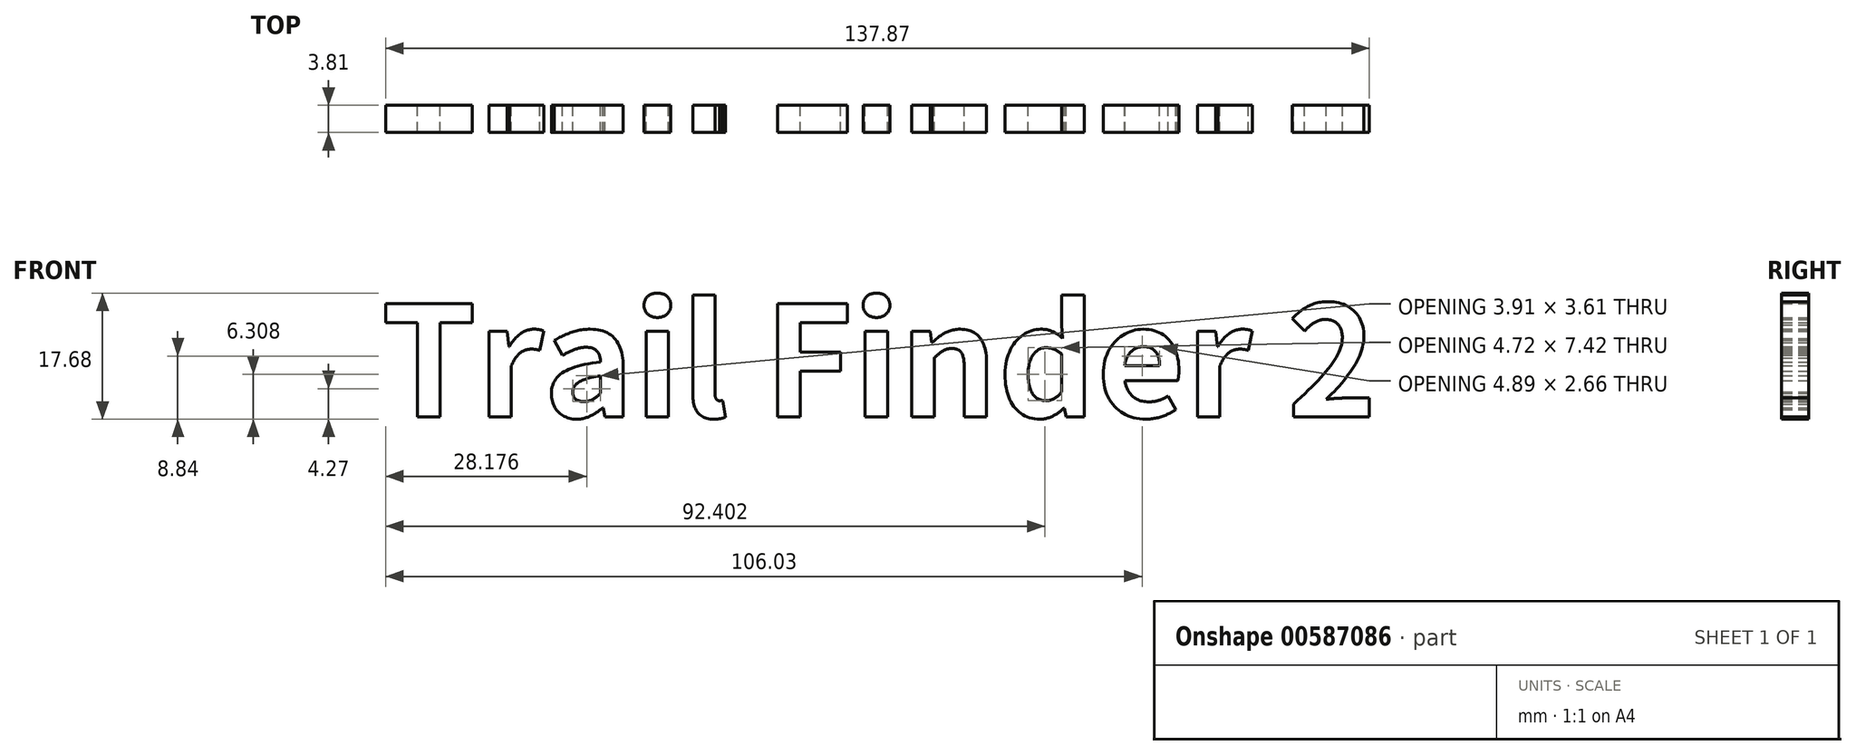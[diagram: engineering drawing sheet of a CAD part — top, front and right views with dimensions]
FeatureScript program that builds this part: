
annotation { "Feature Type Name" : "Feature", "Feature Type Description" : "" }
export const myFeature = defineFeature(function(context is Context, id is Id, definition is map)
    precondition{}
    {
        {
            var Q0;
            Q0=qCreatedBy(makeId("Front.planeOp"),FACE);
            var sketch = newSketch(context, id + "F0", { "sketchPlane" : qUnion([Q0])});
            skText(sketch, "E0", { "text": "Trail Finder 2", "fontName": "NotoSansCJKkr-Bold.otf"});
            const initialGuessF0  = {"E0": [-0.06985, -0.00756, 1, 0, 0.01545]};
            skSetInitialGuess(sketch, initialGuessF0);
            skSolve(sketch);
        }
        {
            var Q0;
            Q0 = qSketchRegion(id + "F0", true);
            extrude(context, id + "F1", {"entities" : qUnion([Q0]), "depth" : 3.8 * mm, "offsetDistance" : 25.4 * mm});
        }
    });
